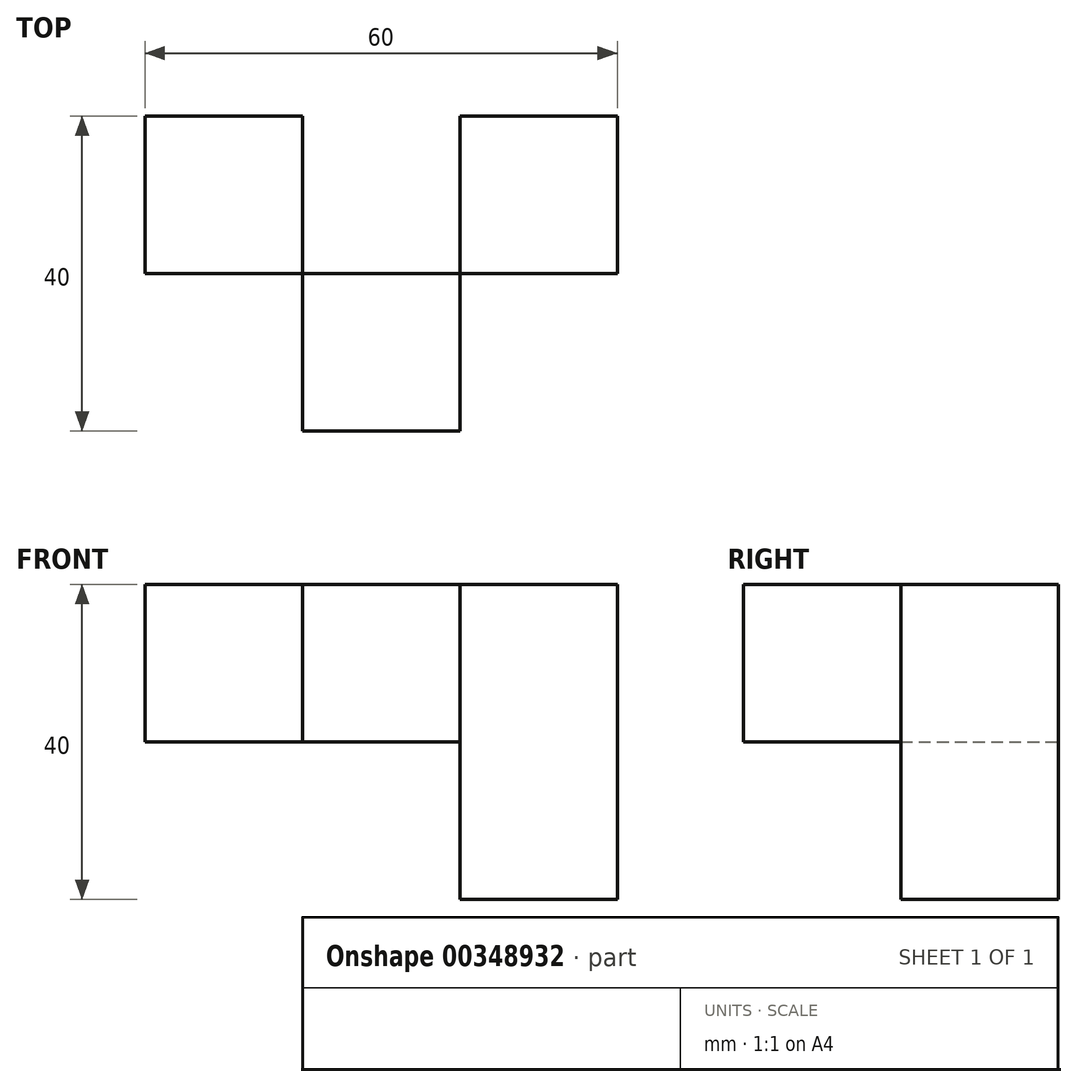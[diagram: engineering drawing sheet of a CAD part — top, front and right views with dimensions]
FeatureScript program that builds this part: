
annotation { "Feature Type Name" : "Feature", "Feature Type Description" : "" }
export const myFeature = defineFeature(function(context is Context, id is Id, definition is map)
    precondition{}
    {
        {
            var Q0;
            Q0=qCreatedBy(makeId("Front.planeOp"),FACE);
            var sketch = newSketch(context, id + "F0", { "sketchPlane" : qUnion([Q0])});
            skLineSegment(sketch, "E0.bottom", {"start": v(-30, 30) * mm, "end": v(30, 30) * mm});
            skLineSegment(sketch, "E0.top", {"start": v(-30, -30) * mm, "end": v(30, -30) * mm});
            skLineSegment(sketch, "E0.left", {"start": v(-30, 30) * mm, "end": v(-30, -30) * mm});
            skLineSegment(sketch, "E0.right", {"start": v(30, 30) * mm, "end": v(30, -30) * mm});
            skPoint(sketch, "E0.middle", {"position": v(0, 0) * mm});
            skLineSegment(sketch, "E1.bottom", {"start": v(-30, 30) * mm, "end": v(-10, 30) * mm});
            skLineSegment(sketch, "E1.top", {"start": v(-30, 10) * mm, "end": v(-10, 10) * mm});
            skLineSegment(sketch, "E1.left", {"start": v(-30, 30) * mm, "end": v(-30, 10) * mm});
            skLineSegment(sketch, "E1.right", {"start": v(-10, 30) * mm, "end": v(-10, 10) * mm});
            skLineSegment(sketch, "E2.bottom", {"start": v(30, 30) * mm, "end": v(10, 30) * mm});
            skLineSegment(sketch, "E2.top", {"start": v(30, -10) * mm, "end": v(10, -10) * mm});
            skLineSegment(sketch, "E2.left", {"start": v(30, 30) * mm, "end": v(30, -10) * mm});
            skLineSegment(sketch, "E2.right", {"start": v(10, 30) * mm, "end": v(10, -10) * mm});
            skSolve(sketch);
        }
        {
            var Q0;
            Q0=makeQuery(id+"F0.imprint","IMPRINT",FACE,{"disambiguationData":[TD([[makeQuery(id+"F0.imprint","IMPRINT",EDGE,{"derivedFrom":sQuery(id+"F0.wireOp",EDGE,"E0.bottom")}),-1.0]])]});
            extrude(context, id + "F1", {"entities" : qUnion([Q0]), "depth" : 20 * mm});
        }
        {
            var Q0;
            Q0=makeQuery(id+"F1.opExtrude","CAP_FACE",FACE,{"disambiguationData":[OSD([sQuery(id+"F0.wireOp",EDGE,"E0.bottom"),sQuery(id+"F0.wireOp",EDGE,"E0.top"),sQuery(id+"F0.wireOp",EDGE,"E0.left"),sQuery(id+"F0.wireOp",EDGE,"E0.right"),sQuery(id+"F0.wireOp",EDGE,"E1.top"),sQuery(id+"F0.wireOp",EDGE,"E1.right"),sQuery(id+"F0.wireOp",EDGE,"E2.top"),sQuery(id+"F0.wireOp",EDGE,"E2.right")])],"isStart":false});
            var sketch = newSketch(context, id + "F2", { "sketchPlane" : qUnion([Q0])});
            skLineSegment(sketch, "E3.bottom", {"start": v(10, 30) * mm, "end": v(-10, 30) * mm});
            skLineSegment(sketch, "E3.top", {"start": v(10, 10) * mm, "end": v(-10, 10) * mm});
            skLineSegment(sketch, "E3.left", {"start": v(10, 30) * mm, "end": v(10, 10) * mm});
            skLineSegment(sketch, "E3.right", {"start": v(-10, 30) * mm, "end": v(-10, 10) * mm});
            skSolve(sketch);
        }
        {
            var Q0;
            Q0 = qSketchRegion(id + "F2", true);
            extrude(context, id + "F3", {"entities" : qUnion([Q0]), "operationType" : NewBodyOperationType.ADD, "depth" : 20 * mm});
        }
        {
            var Q0;
            Q0=makeQuery(id+"F3.boolean.opBoolean","MERGE",FACE,{"derivedFrom":[makeQuery(id+"F1.opExtrude","SWEPT_FACE",FACE,{"disambiguationData":[OSD([sQuery(id+"F0.wireOp",EDGE,"E2.right")])]}),makeQuery(id+"F3.opExtrude","SWEPT_FACE",FACE,{"disambiguationData":[OSD([sQuery(id+"F2.wireOp",EDGE,"E3.left")])]})]});
            var sketch = newSketch(context, id + "F4", { "sketchPlane" : qUnion([Q0])});
            skLineSegment(sketch, "E4.bottom", {"start": v(-20, 10) * mm, "end": v(0, 10) * mm});
            skLineSegment(sketch, "E4.top", {"start": v(-20, -10) * mm, "end": v(0, -10) * mm});
            skLineSegment(sketch, "E4.left", {"start": v(-20, 10) * mm, "end": v(-20, -10) * mm});
            skLineSegment(sketch, "E4.right", {"start": v(0, 10) * mm, "end": v(0, -10) * mm});
            skSolve(sketch);
        }
    });
